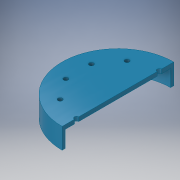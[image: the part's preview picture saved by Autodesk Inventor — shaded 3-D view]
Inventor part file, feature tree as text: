
AUTODESK INVENTOR PART (.ipt)
format: ipt  version: 2019 (Build 230136000, 136)  size: 130,560 bytes
history: native  units: in
note: dims shown in document units (in); Inventor stores cm internally (conversion verified against a paired STEP export)
features: sketch x4, extrude x3, hole x1
ambient origin geometry x8: Origin, YZ Plane, XZ Plane, XY Plane, X Axis, Y Axis, Z Axis, Center Point
bodies: Solid1 (feature_tree)
feature tree (8):
  extrude  "Extrusion1"  Depth=0.25in TaperAngle=0.0deg
  extrude  "Extrusion2"  Depth=1.0in TaperAngle=0.0deg
  extrude  "Extrusion3"  Depth=1.0in
  hole  "Hole1"  [1 undecoded]
  sketch  "Sketch1"  dims[d0=6.75in d1=0.25in d2=0.0in]
  sketch  "Sketch2"  dims[d3=6.375in d4=1.0in d5=0.0in]
  sketch  "Sketch3"  dims[d6=1.0in d7=0.0in d8=5.0in]
  sketch  "Sketch4"  dims[d9=0.2474in d10=3.937in d12=360.0deg d14=0.266in d15=0.75in d16=0.507in d17=0.25in d18=0.5635in d19=1.0in d20=0.8108in]
note: 1 required parameter value undecoded (feature->parameter linkage not recoverable at this tier; creation-order binding heuristic only, values carry confidence <= 0.55)
